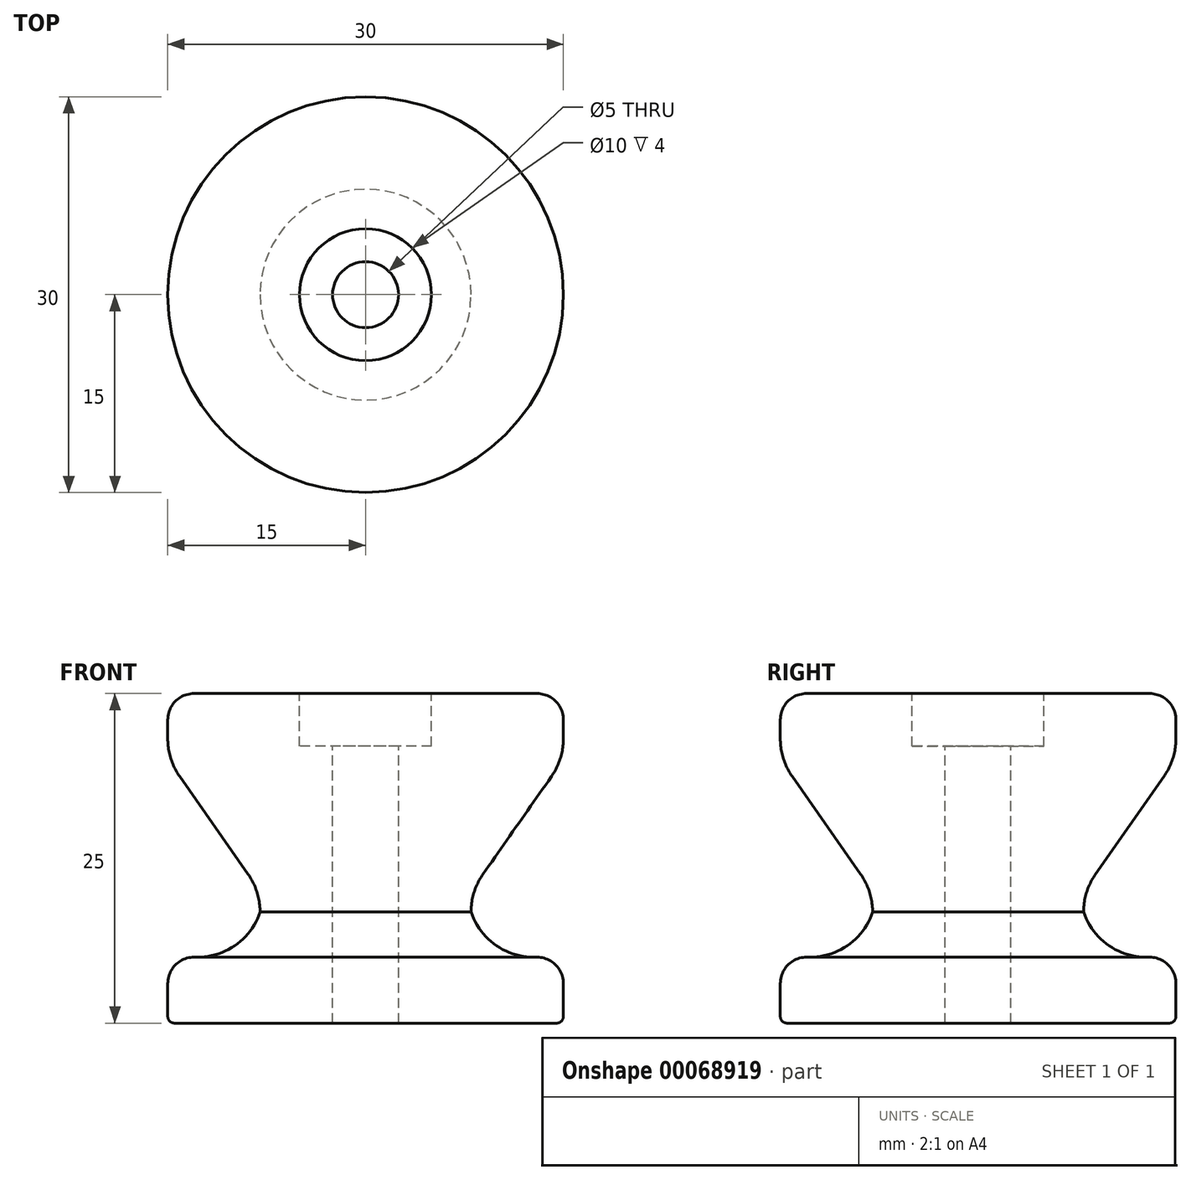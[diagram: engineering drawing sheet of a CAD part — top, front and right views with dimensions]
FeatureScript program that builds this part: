
annotation { "Feature Type Name" : "Feature", "Feature Type Description" : "" }
export const myFeature = defineFeature(function(context is Context, id is Id, definition is map)
    precondition{}
    {
        {
            var Q0;
            Q0=qCreatedBy(makeId("Front.planeOp"),FACE);
            var sketch = newSketch(context, id + "F0", { "sketchPlane" : qUnion([Q0])});
            skLineSegment(sketch, "E0", {"start": v(0, 0) * mm, "end": v(14.5, 0) * mm});
            skLineSegment(sketch, "E1", {"start": v(15, 0.5) * mm, "end": v(15, 3) * mm});
            skLineSegment(sketch, "E2", {"start": v(13, 5) * mm, "end": v(8, 5) * mm});
            skLineSegment(sketch, "E3", {"start": v(8, 5) * mm, "end": v(8, 10) * mm});
            skLineSegment(sketch, "E4", {"start": v(8, 10) * mm, "end": v(15, 20) * mm});
            skLineSegment(sketch, "E5", {"start": v(15, 20) * mm, "end": v(15, 23) * mm});
            skLineSegment(sketch, "E6", {"start": v(13, 25) * mm, "end": v(0, 25) * mm});
            skLineSegment(sketch, "E7", {"start": v(0, 25) * mm, "end": v(0, 0) * mm});
            skPoint(sketch, "E8.visualSharp", {"position": v(15, 25) * mm});
            skArc(sketch, "E8.filletArc", {"start": v(15, 23) * mm, "mid": v(14.41, 24.41) * mm, "end": v(13, 25) * mm});
            skPoint(sketch, "E9.visualSharp", {"position": v(15, 5) * mm});
            skArc(sketch, "E9.filletArc", {"start": v(15, 3) * mm, "mid": v(14.41, 4.41) * mm, "end": v(13, 5) * mm});
            skPoint(sketch, "E10.visualSharp", {"position": v(15, 0) * mm});
            skArc(sketch, "E10.filletArc", {"start": v(14.5, 0) * mm, "mid": v(14.85, 0.15) * mm, "end": v(15, 0.5) * mm});
            skSolve(sketch);
        }
        {
            var Q0;
            Q0=makeQuery(id+"F0.imprint","IMPRINT",FACE,{"disambiguationData":[TD([[makeQuery(id+"F0.imprint","IMPRINT",EDGE,{"derivedFrom":sQuery(id+"F0.wireOp",EDGE,"E0")}),1.0]])]});
            var Q1;
            Q1=sQuery(id+"F0.wireOp",EDGE,"E7");
            revolve(context, id + "F1", {"entities" : qUnion([Q0]), "axis" : qUnion([Q1]), "revolveType" : RevolveType.FULL});
        }
        {
            var Q0;
            Q0=makeQuery(id+"F1.opRevolve","SWEPT_FACE",FACE,{"disambiguationData":[OSD([sQuery(id+"F0.wireOp",EDGE,"E4")])]});
            fillet(context, id + "F2", {"entities" : qUnion([Q0]), "radius" : 5 * mm, "tangentPropagation" : true, "allowEdgeOverflow" : false});
        }
        {
            var Q0;
            Q0=makeQuery(id+"F1.opRevolve","SWEPT_FACE",FACE,{"disambiguationData":[OSD([sQuery(id+"F0.wireOp",EDGE,"E3")])]});
            fillet(context, id + "F3", {"entities" : qUnion([Q0]), "radius" : 5 * mm, "tangentPropagation" : true, "allowEdgeOverflow" : false});
        }
        {
            var Q0;
            Q0=makeQuery(id+"F1.opRevolve","SWEPT_FACE",FACE,{"disambiguationData":[OSD([sQuery(id+"F0.wireOp",EDGE,"E6")])]});
            var sketch = newSketch(context, id + "F4", { "sketchPlane" : qUnion([Q0])});
            skCircle(sketch, "E11", {"center": v(0, 0) * mm, "radius": 2.5 * mm});
            skSolve(sketch);
        }
        {
            var Q0;
            Q0 = qSketchRegion(id + "F4", true);
            extrude(context, id + "F5", {"entities" : qUnion([Q0]), "operationType" : NewBodyOperationType.REMOVE, "endBound" : BoundingType.THROUGH_ALL, "oppositeDirection" : true, "depth" : 25 * mm});
        }
        {
            var Q0;
            Q0=sQuery(id+"F4.wireOp",VERTEX,"E11.center");
            var Q1;
            Q1=makeQuery(id+"F1.opRevolve","SWEPT_BODY",BODY,{"disambiguationData":[OSD([sQuery(id+"F0.wireOp",EDGE,"E0"),sQuery(id+"F0.wireOp",EDGE,"E1"),sQuery(id+"F0.wireOp",EDGE,"E2"),sQuery(id+"F0.wireOp",EDGE,"E3"),sQuery(id+"F0.wireOp",EDGE,"E4"),sQuery(id+"F0.wireOp",EDGE,"E5"),sQuery(id+"F0.wireOp",EDGE,"E6"),sQuery(id+"F0.wireOp",EDGE,"E7"),sQuery(id+"F0.wireOp",EDGE,"E8.filletArc"),sQuery(id+"F0.wireOp",EDGE,"E9.filletArc")])]});
            hole(context, id + "F6", {"style" : HoleStyle.C_BORE, "holeDiameter" : 5 * mm, "cBoreDiameter" : 10 * mm, "cBoreDepth" : 4 * mm, "endStyle" : HoleEndStyle.THROUGH, "locations" : qUnion([Q0]), "scope" : qUnion([Q1])});
        }
    });
